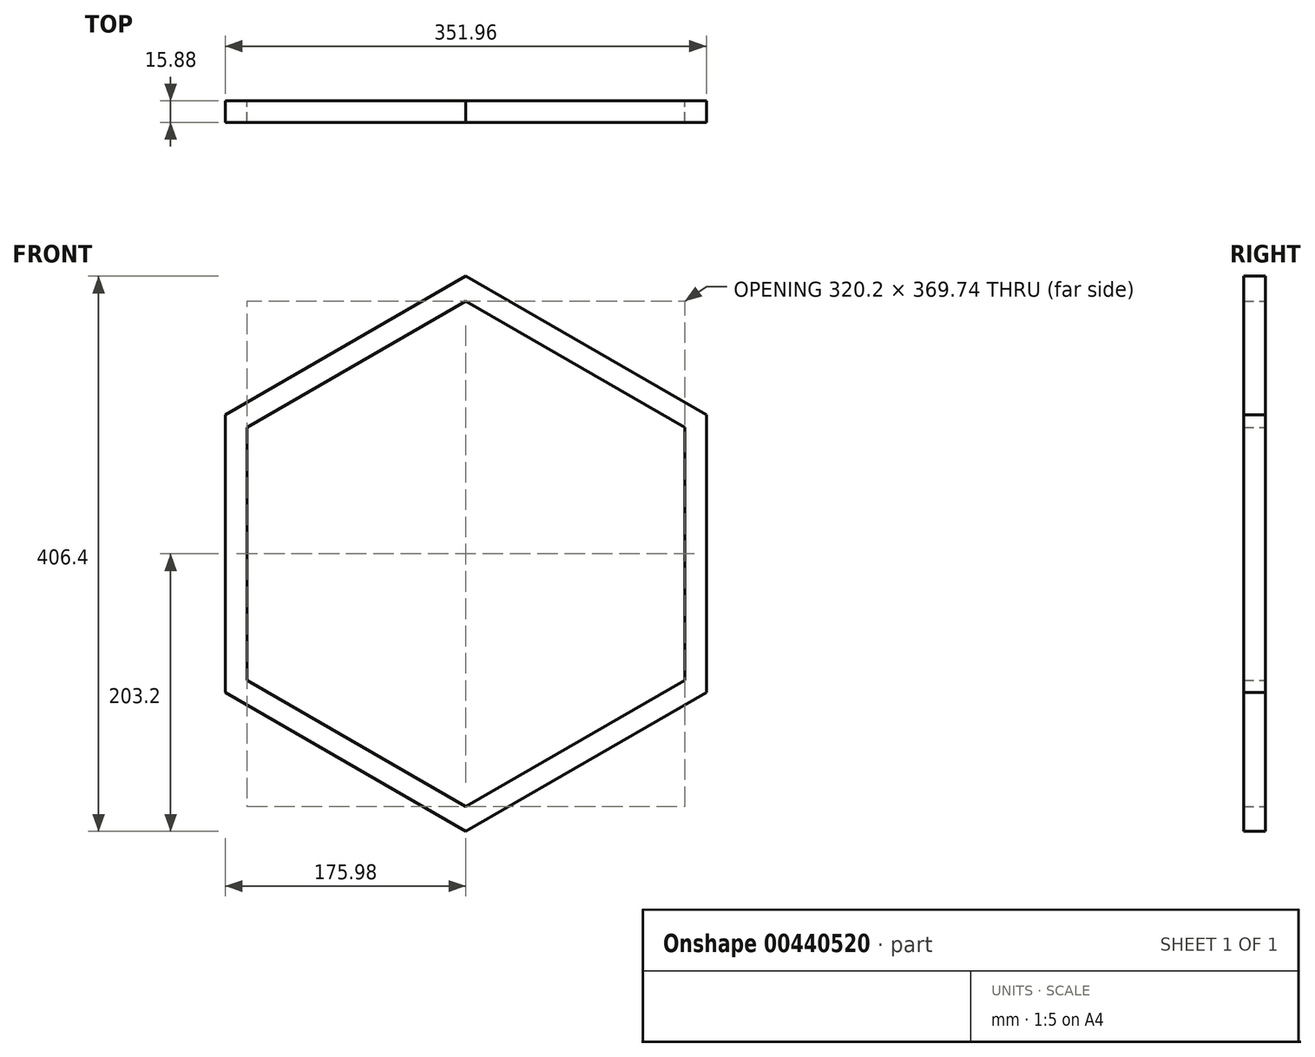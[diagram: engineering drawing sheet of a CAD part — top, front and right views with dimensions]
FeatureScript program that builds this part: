
annotation { "Feature Type Name" : "Feature", "Feature Type Description" : "" }
export const myFeature = defineFeature(function(context is Context, id is Id, definition is map)
    precondition{}
    {
        {
            var Q0;
            Q0=qCreatedBy(makeId("Front.planeOp"),FACE);
            var sketch = newSketch(context, id + "F0", { "sketchPlane" : qUnion([Q0])});
            skCircle(sketch, "E0.cCircle", {"center": v(0, 0) * mm, "radius": 203.2 * mm, "construction": true});
            skLineSegment(sketch, "E0.0", {"start": v(0, 203.2) * mm, "end": v(175.98, 101.6) * mm});
            skLineSegment(sketch, "E0.1", {"start": v(175.98, 101.6) * mm, "end": v(175.98, -101.6) * mm});
            skLineSegment(sketch, "E0.2", {"start": v(175.98, -101.6) * mm, "end": v(0, -203.2) * mm});
            skLineSegment(sketch, "E0.3", {"start": v(0, -203.2) * mm, "end": v(-175.98, -101.6) * mm});
            skLineSegment(sketch, "E0.4", {"start": v(-175.98, -101.6) * mm, "end": v(-175.98, 101.6) * mm});
            skLineSegment(sketch, "E0.5", {"start": v(-175.98, 101.6) * mm, "end": v(0, 203.2) * mm});
            skLineSegment(sketch, "E1.0", {"start": v(160.1, 92.43) * mm, "end": v(160.1, -92.43) * mm});
            skLineSegment(sketch, "E1.1", {"start": v(0, -184.87) * mm, "end": v(-160.1, -92.43) * mm});
            skLineSegment(sketch, "E1.2", {"start": v(-160.1, -92.43) * mm, "end": v(-160.1, 92.43) * mm});
            skLineSegment(sketch, "E1.3", {"start": v(160.1, -92.43) * mm, "end": v(0, -184.87) * mm});
            skLineSegment(sketch, "E1.4", {"start": v(-160.1, 92.43) * mm, "end": v(0, 184.87) * mm});
            skLineSegment(sketch, "E1.5", {"start": v(0, 184.87) * mm, "end": v(160.1, 92.43) * mm});
            skSolve(sketch);
        }
        {
            var Q0;
            Q0 = qSketchRegion(id + "F0", true);
            extrude(context, id + "F1", {"entities" : qUnion([Q0]), "depth" : 15.88 * mm});
        }
    });
